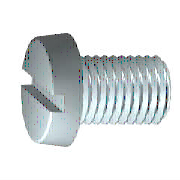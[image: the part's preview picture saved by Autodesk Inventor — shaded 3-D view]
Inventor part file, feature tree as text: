
AUTODESK INVENTOR PART (.ipt)
format: ipt  version: 2023 (Build 270158000, 158)  size: 177,664 bytes
history: native  units: mm (DEFAULTED — no unit token found)
features: sketch x2, extrude x1, plane x1
ambient origin geometry x7: Origin, YZ Plane, XZ Plane, X Axis, Y Axis, Z Axis, Center Point
bodies: Solid1 (feature_tree), Body (feature_tree)
feature tree (4):
  sketch  "Sketch2"  dims[d2=0.49086mm d3=3.3mm d4=5.0mm d5=4.566987mm d8=90.0deg d7=0.0mm d9=8.5mm d10=0.872665mm d11=1.2mm d12=8.5mm d14=0.2mm d15=38.0mm d16=0.0mm d17=0.433015mm d18=0.49086mm d19=1.3mm d20=0.0mm d36=45.0deg d37=0.0mm d39=0.0mm]
  extrude  "Slot"  Depth=38.0mm
  plane  "Work Plane1"
  sketch  "Sketch1"  dims[d0=50.0mm d1=38.0mm]
